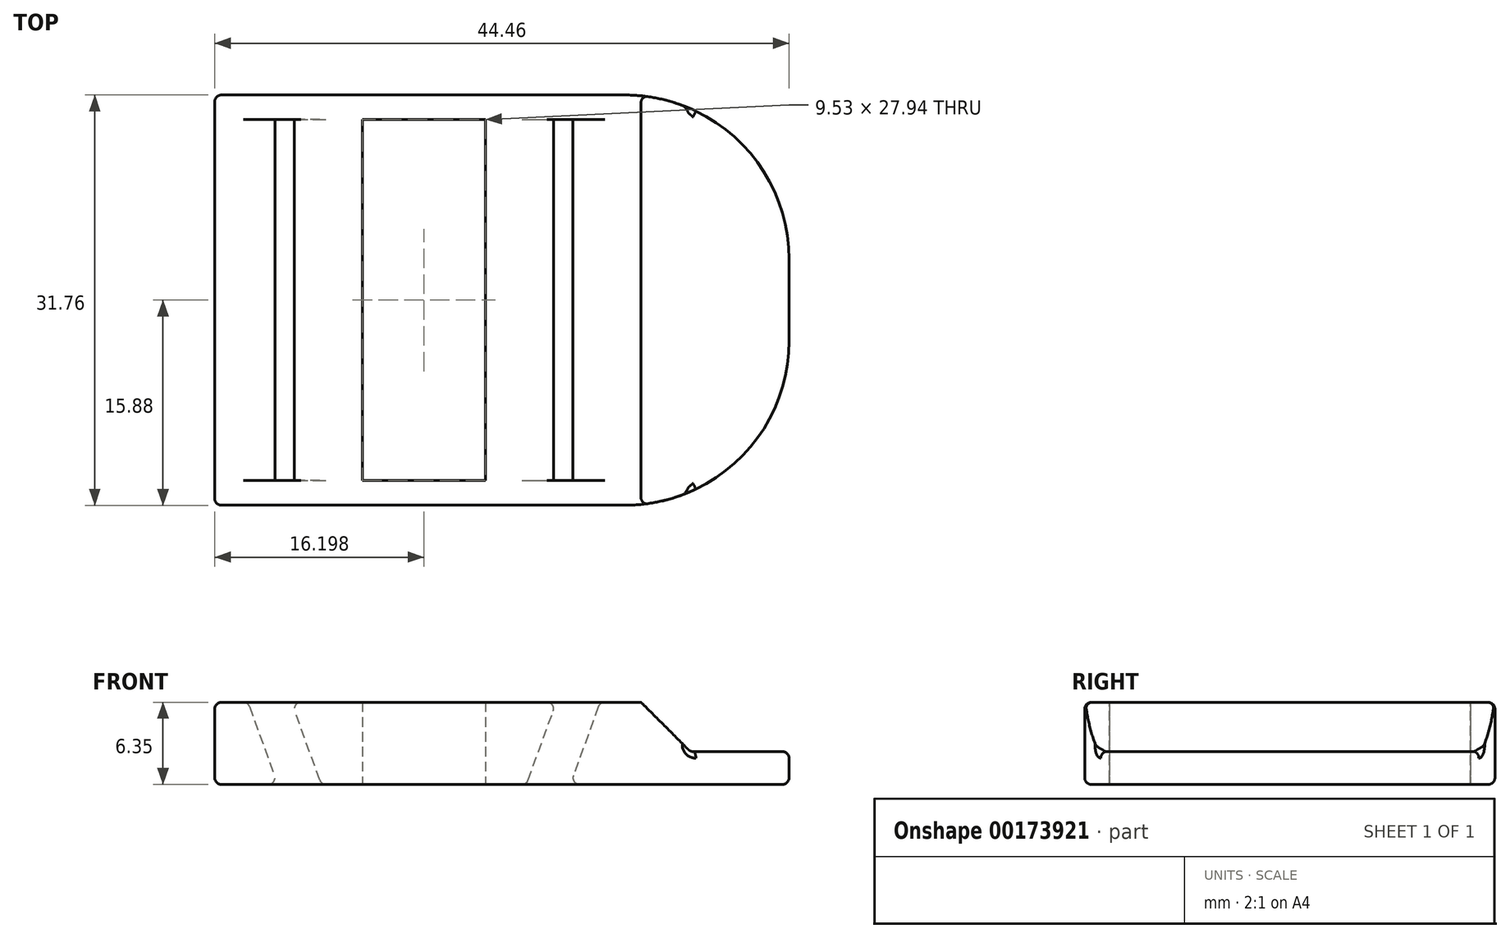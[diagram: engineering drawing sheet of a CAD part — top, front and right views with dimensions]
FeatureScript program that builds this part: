
annotation { "Feature Type Name" : "Feature", "Feature Type Description" : "" }
export const myFeature = defineFeature(function(context is Context, id is Id, definition is map)
    precondition{}
    {
        {
            var Q0;
            Q0=qCreatedBy(makeId("Top.planeOp"),FACE);
            var sketch = newSketch(context, id + "F0", { "sketchPlane" : qUnion([Q0])});
            skLineSegment(sketch, "E0.bottom", {"start": v(-22.23, 15.88) * mm, "end": v(22.23, 15.88) * mm});
            skLineSegment(sketch, "E0.top", {"start": v(-22.23, -15.88) * mm, "end": v(22.22, -15.88) * mm});
            skLineSegment(sketch, "E0.left", {"start": v(-22.23, 15.88) * mm, "end": v(-22.23, -15.87) * mm});
            skLineSegment(sketch, "E0.right", {"start": v(22.23, 15.88) * mm, "end": v(22.22, -15.87) * mm});
            skPoint(sketch, "E0.middle", {"position": v(0, 0) * mm});
            skSolve(sketch);
        }
        {
            var Q0;
            Q0 = qSketchRegion(id + "F0", true);
            extrude(context, id + "F1", {"entities" : qUnion([Q0]), "depth" : 6.35 * mm});
        }
        {
            var Q0;
            Q0=qCreatedBy(makeId("Front.planeOp"),FACE);
            var sketch = newSketch(context, id + "F2", { "sketchPlane" : qUnion([Q0])});
            skLineSegment(sketch, "E1.bottom", {"start": v(-10.8, 6.35) * mm, "end": v(-1.27, 6.35) * mm});
            skLineSegment(sketch, "E1.top", {"start": v(-10.8, 0) * mm, "end": v(-1.27, 0) * mm});
            skLineSegment(sketch, "E1.left", {"start": v(-10.8, 6.35) * mm, "end": v(-10.8, 0) * mm});
            skLineSegment(sketch, "E1.right", {"start": v(-1.27, 6.35) * mm, "end": v(-1.27, 0) * mm});
            skLineSegment(sketch, "E2", {"start": v(-20.15, 7.69) * mm, "end": v(-16.86, -1.34) * mm});
            skLineSegment(sketch, "E3", {"start": v(-16.86, -1.34) * mm, "end": v(-13.88, -0.25) * mm});
            skLineSegment(sketch, "E4", {"start": v(-13.88, -0.25) * mm, "end": v(-17.16, 8.78) * mm});
            skLineSegment(sketch, "E5", {"start": v(-17.16, 8.78) * mm, "end": v(-20.15, 7.69) * mm});
            skPoint(sketch, "E6", {"position": v(-18.5, 3.18) * mm});
            skPoint(sketch, "E7", {"position": v(-13.97, 0) * mm});
            skLineSegment(sketch, "E8", {"start": v(-6.03, 6.35) * mm, "end": v(-6.03, 0) * mm, "construction": true});
            skPoint(sketch, "E9.MirrorP", {"position": v(6.44, 3.18) * mm});
            skPoint(sketch, "E10.MirrorP", {"position": v(1.9, 0) * mm});
            skLineSegment(sketch, "E11.MirrorCS", {"start": v(4.8, -1.34) * mm, "end": v(1.81, -0.25) * mm});
            skLineSegment(sketch, "E12.MirrorCS", {"start": v(5.1, 8.78) * mm, "end": v(8.08, 7.69) * mm});
            skLineSegment(sketch, "E13.MirrorCS", {"start": v(1.81, -0.25) * mm, "end": v(5.1, 8.78) * mm});
            skLineSegment(sketch, "E14.MirrorCS", {"start": v(8.08, 7.69) * mm, "end": v(4.8, -1.34) * mm});
            skSolve(sketch);
        }
        {
            var Q0;
            Q0 = qSketchRegion(id + "F2", true);
            extrude(context, id + "F3", {"entities" : qUnion([Q0]), "operationType" : NewBodyOperationType.REMOVE, "endBound" : BoundingType.SYMMETRIC, "oppositeDirection" : true, "depth" : 27.94 * mm});
        }
        {
            var Q0;
            Q0=makeQuery(id+"F1.opExtrude","SWEPT_FACE",FACE,{"disambiguationData":[OSD([sQuery(id+"F0.wireOp",EDGE,"E0.top")])]});
            var sketch = newSketch(context, id + "F4", { "sketchPlane" : qUnion([Q0])});
            skLineSegment(sketch, "E15", {"start": v(10.77, 6.35) * mm, "end": v(14.58, 2.54) * mm});
            skLineSegment(sketch, "E16", {"start": v(14.58, 2.54) * mm, "end": v(22.22, 2.54) * mm});
            skLineSegment(sketch, "E17", {"start": v(22.22, 6.35) * mm, "end": v(10.77, 6.35) * mm});
            skLineSegment(sketch, "E18", {"start": v(22.22, 2.54) * mm, "end": v(22.22, 6.35) * mm});
            skSolve(sketch);
        }
        {
            var Q0;
            Q0 = qSketchRegion(id + "F4", true);
            extrude(context, id + "F5", {"entities" : qUnion([Q0]), "operationType" : NewBodyOperationType.REMOVE, "endBound" : BoundingType.THROUGH_ALL, "oppositeDirection" : true, "depth" : 25.4 * mm});
        }
        {
            var Q0;
            Q0=makeQuery(id+"F1.opExtrude","SWEPT_EDGE",EDGE,{"disambiguationData":[OSD([sQuery(id+"F0.wireOp",EDGE,"E0.top"),sQuery(id+"F0.wireOp",EDGE,"E0.right")])]});
            var Q1;
            Q1=makeQuery(id+"F1.opExtrude","SWEPT_EDGE",EDGE,{"disambiguationData":[OSD([sQuery(id+"F0.wireOp",EDGE,"E0.bottom"),sQuery(id+"F0.wireOp",EDGE,"E0.right")])]});
            fillet(context, id + "F6", {"entities" : qUnion([Q0, Q1]), "radius" : 12.7 * mm, "tangentPropagation" : true, "allowEdgeOverflow" : false});
        }
        {
            var Q0;
            Q0=makeQuery(id+"F3.boolean.opBoolean","INTERSECT",EDGE,{"derivedFrom":[makeQuery(id+"F1.opExtrude","CAP_FACE",FACE,{"disambiguationData":[OSD([sQuery(id+"F0.wireOp",EDGE,"E0.bottom"),sQuery(id+"F0.wireOp",EDGE,"E0.top"),sQuery(id+"F0.wireOp",EDGE,"E0.left"),sQuery(id+"F0.wireOp",EDGE,"E0.right")])],"isStart":false}),makeQuery(id+"F3.opExtrude","SWEPT_FACE",FACE,{"disambiguationData":[OSD([sQuery(id+"F2.wireOp",EDGE,"E4")])]})]});
            var Q1;
            Q1=makeQuery(id+"F3.boolean.opBoolean","INTERSECT",EDGE,{"derivedFrom":[makeQuery(id+"F1.opExtrude","CAP_FACE",FACE,{"disambiguationData":[OSD([sQuery(id+"F0.wireOp",EDGE,"E0.bottom"),sQuery(id+"F0.wireOp",EDGE,"E0.top"),sQuery(id+"F0.wireOp",EDGE,"E0.left"),sQuery(id+"F0.wireOp",EDGE,"E0.right")])],"isStart":false}),makeQuery(id+"F3.opExtrude","SWEPT_FACE",FACE,{"disambiguationData":[OSD([sQuery(id+"F2.wireOp",EDGE,"E2")])]})]});
            var Q2;
            Q2=makeQuery(id+"F3.boolean.opBoolean","INTERSECT",EDGE,{"derivedFrom":[makeQuery(id+"F1.opExtrude","CAP_FACE",FACE,{"disambiguationData":[OSD([sQuery(id+"F0.wireOp",EDGE,"E0.bottom"),sQuery(id+"F0.wireOp",EDGE,"E0.top"),sQuery(id+"F0.wireOp",EDGE,"E0.left"),sQuery(id+"F0.wireOp",EDGE,"E0.right")])],"isStart":true}),makeQuery(id+"F3.opExtrude","SWEPT_FACE",FACE,{"disambiguationData":[OSD([sQuery(id+"F2.wireOp",EDGE,"E2")])]})]});
            var Q3;
            Q3=makeQuery(id+"F3.boolean.opBoolean","COPY",EDGE,{"derivedFrom":makeQuery(id+"F3.opExtrude","SWEPT_EDGE",EDGE,{"disambiguationData":[OSD([sQuery(id+"F2.wireOp",EDGE,"E1.bottom"),sQuery(id+"F2.wireOp",EDGE,"E1.left")])]})});
            var Q4;
            Q4=makeQuery(id+"F3.boolean.opBoolean","COPY",EDGE,{"derivedFrom":makeQuery(id+"F3.opExtrude","SWEPT_EDGE",EDGE,{"disambiguationData":[OSD([sQuery(id+"F2.wireOp",EDGE,"E1.bottom"),sQuery(id+"F2.wireOp",EDGE,"E1.right")])]})});
            var Q5;
            Q5=makeQuery(id+"F3.boolean.opBoolean","INTERSECT",EDGE,{"derivedFrom":[makeQuery(id+"F1.opExtrude","CAP_FACE",FACE,{"disambiguationData":[OSD([sQuery(id+"F0.wireOp",EDGE,"E0.bottom"),sQuery(id+"F0.wireOp",EDGE,"E0.top"),sQuery(id+"F0.wireOp",EDGE,"E0.left"),sQuery(id+"F0.wireOp",EDGE,"E0.right")])],"isStart":false}),makeQuery(id+"F3.opExtrude","SWEPT_FACE",FACE,{"disambiguationData":[OSD([sQuery(id+"F2.wireOp",EDGE,"E13.MirrorCS")])]})]});
            var Q6;
            Q6=makeQuery(id+"F5.boolean.opBoolean","INTERSECT",EDGE,{"derivedFrom":[makeQuery(id+"F3.boolean.opBoolean","COPY",FACE,{"derivedFrom":makeQuery(id+"F3.opExtrude","SWEPT_FACE",FACE,{"disambiguationData":[OSD([sQuery(id+"F2.wireOp",EDGE,"E14.MirrorCS")])]})}),makeQuery(id+"F5.opExtrude","SWEPT_FACE",FACE,{"disambiguationData":[OSD([sQuery(id+"F4.wireOp",EDGE,"E15")])]})]});
            var Q7;
            Q7=makeQuery(id+"F3.boolean.opBoolean","INTERSECT",EDGE,{"derivedFrom":[makeQuery(id+"F1.opExtrude","CAP_FACE",FACE,{"disambiguationData":[OSD([sQuery(id+"F0.wireOp",EDGE,"E0.bottom"),sQuery(id+"F0.wireOp",EDGE,"E0.top"),sQuery(id+"F0.wireOp",EDGE,"E0.left"),sQuery(id+"F0.wireOp",EDGE,"E0.right")])],"isStart":true}),makeQuery(id+"F3.opExtrude","SWEPT_FACE",FACE,{"disambiguationData":[OSD([sQuery(id+"F2.wireOp",EDGE,"E4")])]})]});
            var Q8;
            Q8=makeQuery(id+"F3.boolean.opBoolean","COPY",EDGE,{"derivedFrom":makeQuery(id+"F3.opExtrude","SWEPT_EDGE",EDGE,{"disambiguationData":[OSD([sQuery(id+"F2.wireOp",EDGE,"E1.top"),sQuery(id+"F2.wireOp",EDGE,"E1.left")])]})});
            var Q9;
            Q9=makeQuery(id+"F3.boolean.opBoolean","COPY",EDGE,{"derivedFrom":makeQuery(id+"F3.opExtrude","SWEPT_EDGE",EDGE,{"disambiguationData":[OSD([sQuery(id+"F2.wireOp",EDGE,"E1.top"),sQuery(id+"F2.wireOp",EDGE,"E1.right")])]})});
            var Q10;
            Q10=makeQuery(id+"F3.boolean.opBoolean","INTERSECT",EDGE,{"derivedFrom":[makeQuery(id+"F1.opExtrude","CAP_FACE",FACE,{"disambiguationData":[OSD([sQuery(id+"F0.wireOp",EDGE,"E0.bottom"),sQuery(id+"F0.wireOp",EDGE,"E0.top"),sQuery(id+"F0.wireOp",EDGE,"E0.left"),sQuery(id+"F0.wireOp",EDGE,"E0.right")])],"isStart":true}),makeQuery(id+"F3.opExtrude","SWEPT_FACE",FACE,{"disambiguationData":[OSD([sQuery(id+"F2.wireOp",EDGE,"E13.MirrorCS")])]})]});
            var Q11;
            Q11=makeQuery(id+"F3.boolean.opBoolean","INTERSECT",EDGE,{"derivedFrom":[makeQuery(id+"F1.opExtrude","CAP_FACE",FACE,{"disambiguationData":[OSD([sQuery(id+"F0.wireOp",EDGE,"E0.bottom"),sQuery(id+"F0.wireOp",EDGE,"E0.top"),sQuery(id+"F0.wireOp",EDGE,"E0.left"),sQuery(id+"F0.wireOp",EDGE,"E0.right")])],"isStart":true}),makeQuery(id+"F3.opExtrude","SWEPT_FACE",FACE,{"disambiguationData":[OSD([sQuery(id+"F2.wireOp",EDGE,"E14.MirrorCS")])]})]});
            var Q12;
            Q12=makeQuery(id+"F3.boolean.opBoolean","INTERSECT",EDGE,{"derivedFrom":[makeQuery(id+"F1.opExtrude","CAP_FACE",FACE,{"disambiguationData":[OSD([sQuery(id+"F0.wireOp",EDGE,"E0.bottom"),sQuery(id+"F0.wireOp",EDGE,"E0.top"),sQuery(id+"F0.wireOp",EDGE,"E0.left"),sQuery(id+"F0.wireOp",EDGE,"E0.right")])],"isStart":false}),makeQuery(id+"F3.opExtrude","SWEPT_FACE",FACE,{"disambiguationData":[OSD([sQuery(id+"F2.wireOp",EDGE,"E14.MirrorCS")])]})]});
            var Q13;
            Q13=makeQuery(id+"F5.boolean.opBoolean","COPY",EDGE,{"derivedFrom":makeQuery(id+"F5.opExtrude","SWEPT_EDGE",EDGE,{"disambiguationData":[OSD([sQuery(id+"F4.wireOp",EDGE,"E15"),sQuery(id+"F4.wireOp",EDGE,"E16")])]})});
            var Q14;
            Q14=makeQuery(id+"F6.opFillet","BLEND_EDGE",EDGE,{"blendedFrom":[makeQuery(id+"F1.opExtrude","SWEPT_EDGE",EDGE,{"disambiguationData":[OSD([sQuery(id+"F0.wireOp",EDGE,"E0.top"),sQuery(id+"F0.wireOp",EDGE,"E0.right")])]}),makeQuery(id+"F5.boolean.opBoolean","COPY",FACE,{"derivedFrom":makeQuery(id+"F5.opExtrude","SWEPT_FACE",FACE,{"disambiguationData":[OSD([sQuery(id+"F4.wireOp",EDGE,"E16")])]})})],"blendedInto":[makeQuery(id+"F5.boolean.opBoolean","COPY",FACE,{"derivedFrom":makeQuery(id+"F5.opExtrude","SWEPT_FACE",FACE,{"disambiguationData":[OSD([sQuery(id+"F4.wireOp",EDGE,"E16")])]})})]});
            var Q15;
            {var subQ0=sQuery(id+"F0.wireOp",EDGE,"E0.right");var subQ1=sQuery(id+"F0.wireOp",EDGE,"E0.top");Q15=makeQuery(id+"F6.opFillet","BLEND_EDGE",EDGE,{"blendedFrom":[makeQuery(id+"F1.opExtrude","SWEPT_EDGE",EDGE,{"disambiguationData":[OSD([subQ1,subQ0])]}),makeQuery(id+"F1.opExtrude","CAP_FACE",FACE,{"disambiguationData":[OSD([sQuery(id+"F0.wireOp",EDGE,"E0.bottom"),subQ1,sQuery(id+"F0.wireOp",EDGE,"E0.left"),subQ0])],"isStart":true})],"blendedInto":[makeQuery(id+"F1.opExtrude","CAP_FACE",FACE,{"disambiguationData":[OSD([sQuery(id+"F0.wireOp",EDGE,"E0.bottom"),subQ1,sQuery(id+"F0.wireOp",EDGE,"E0.left"),subQ0])],"isStart":true})]});}
            var Q16;
            Q16=makeQuery(id+"F1.opExtrude","CAP_EDGE",EDGE,{"disambiguationData":[OSD([sQuery(id+"F0.wireOp",EDGE,"E0.left")])],"isStart":true});
            var Q17;
            Q17=makeQuery(id+"F1.opExtrude","CAP_EDGE",EDGE,{"disambiguationData":[OSD([sQuery(id+"F0.wireOp",EDGE,"E0.bottom")])],"isStart":false});
            var Q18;
            Q18=makeQuery(id+"F1.opExtrude","CAP_EDGE",EDGE,{"disambiguationData":[OSD([sQuery(id+"F0.wireOp",EDGE,"E0.left")])],"isStart":false});
            var Q19;
            Q19=makeQuery(id+"F1.opExtrude","CAP_EDGE",EDGE,{"disambiguationData":[OSD([sQuery(id+"F0.wireOp",EDGE,"E0.top")])],"isStart":false});
            var Q20;
            Q20=makeQuery(id+"F1.opExtrude","SWEPT_EDGE",EDGE,{"disambiguationData":[OSD([sQuery(id+"F0.wireOp",EDGE,"E0.top"),sQuery(id+"F0.wireOp",EDGE,"E0.left")])]});
            var Q21;
            Q21=makeQuery(id+"F1.opExtrude","SWEPT_EDGE",EDGE,{"disambiguationData":[OSD([sQuery(id+"F0.wireOp",EDGE,"E0.bottom"),sQuery(id+"F0.wireOp",EDGE,"E0.left")])]});
            fillet(context, id + "F7", {"entities" : qUnion([Q0, Q1, Q2, Q3, Q4, Q5, Q6, Q7, Q8, Q9, Q10, Q11, Q12, Q13, Q14, Q15, Q16, Q17, Q18, Q19, Q20, Q21]), "radius" : 0.5 * mm, "tangentPropagation" : true, "allowEdgeOverflow" : false});
        }
    });
